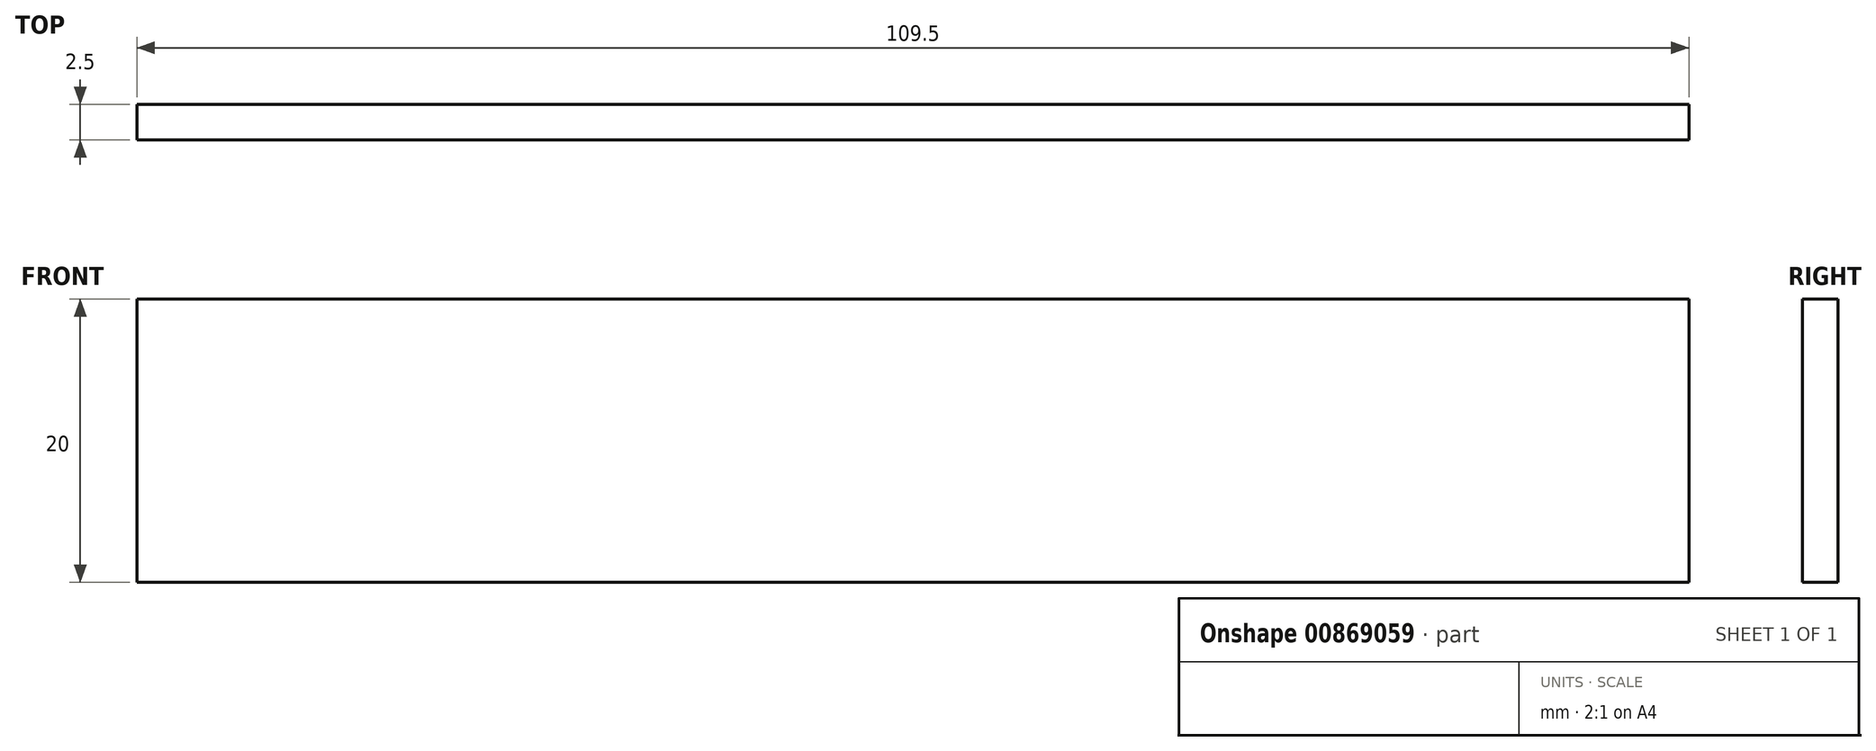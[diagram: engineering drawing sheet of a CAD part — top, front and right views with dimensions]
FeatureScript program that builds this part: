
annotation { "Feature Type Name" : "Feature", "Feature Type Description" : "" }
export const myFeature = defineFeature(function(context is Context, id is Id, definition is map)
    precondition{}
    {
        {
            var Q0;
            Q0=qCreatedBy(makeId("Front.planeOp"),FACE);
            var sketch = newSketch(context, id + "F0", { "sketchPlane" : qUnion([Q0])});
            skLineSegment(sketch, "E0.bottom", {"start": v(0, 0) * mm, "end": v(109.5, 0) * mm});
            skLineSegment(sketch, "E0.top", {"start": v(0, 20) * mm, "end": v(109.5, 20) * mm});
            skLineSegment(sketch, "E0.left", {"start": v(0, 0) * mm, "end": v(0, 20) * mm});
            skLineSegment(sketch, "E0.right", {"start": v(109.5, 0) * mm, "end": v(109.5, 20) * mm});
            skSolve(sketch);
        }
        {
            var Q0;
            Q0=makeQuery(id+"F0.imprint","IMPRINT",FACE,{"disambiguationData":[TD([[makeQuery(id+"F0.imprint","IMPRINT",EDGE,{"derivedFrom":sQuery(id+"F0.wireOp",EDGE,"E0.bottom")}),1.0]])]});
            extrude(context, id + "F1", {"entities" : qUnion([Q0]), "depth" : 2.5 * mm, "offsetDistance" : 25 * mm});
        }
    });
